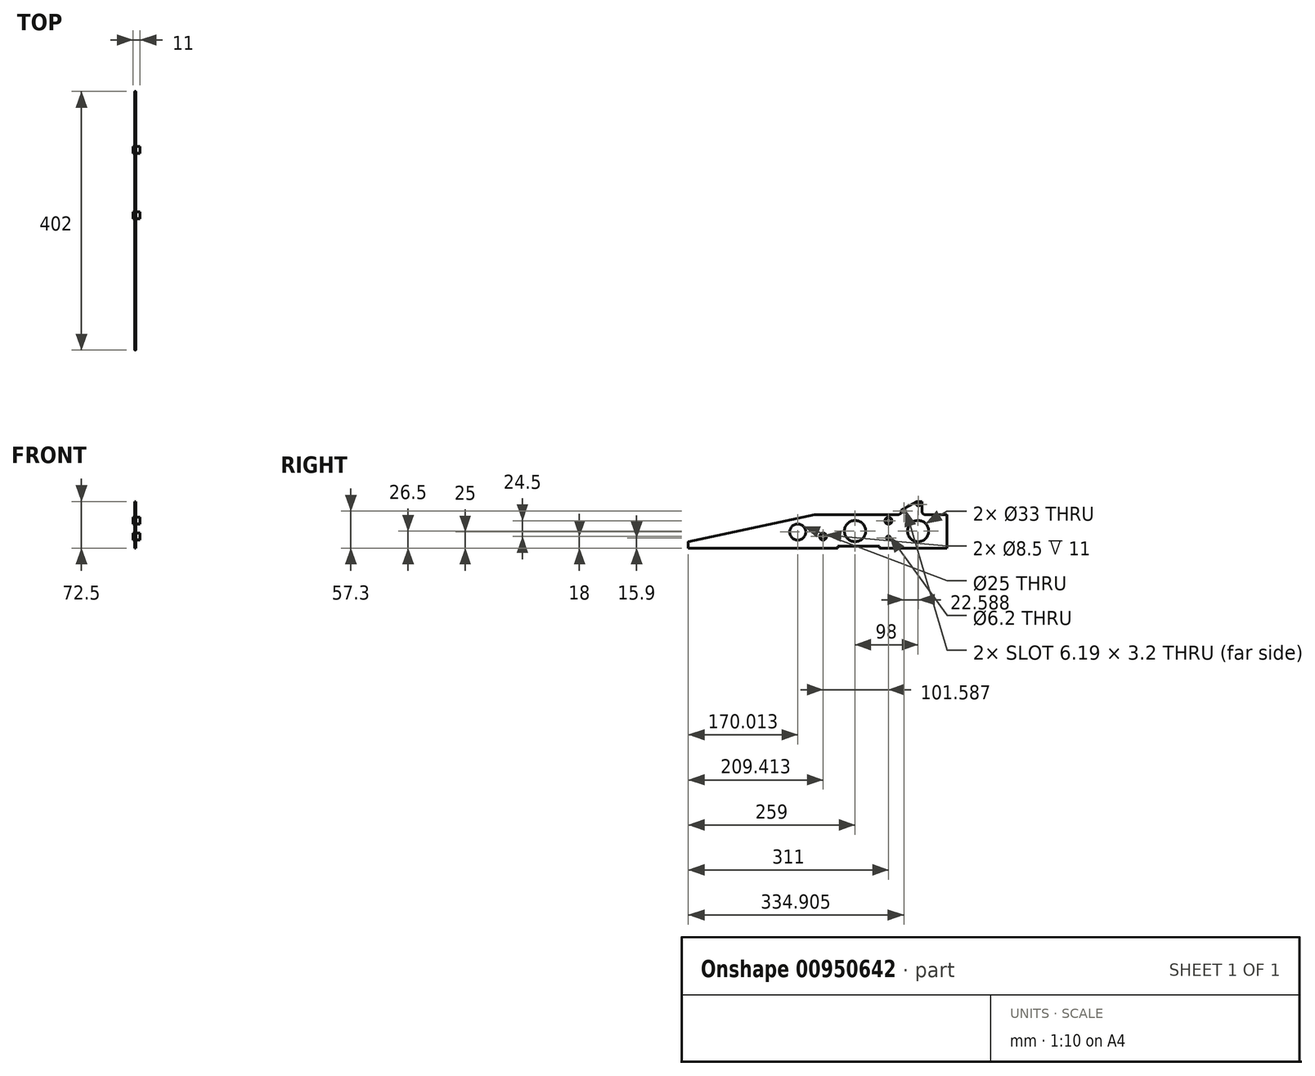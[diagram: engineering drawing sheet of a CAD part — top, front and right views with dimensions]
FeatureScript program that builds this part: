
annotation { "Feature Type Name" : "Feature", "Feature Type Description" : "" }
export const myFeature = defineFeature(function(context is Context, id is Id, definition is map)
    precondition{}
    {
        {
            var Q0;
            Q0=qCreatedBy(makeId("Right.planeOp"),FACE);
            var sketch = newSketch(context, id + "F0", { "sketchPlane" : qUnion([Q0])});
            skLineSegment(sketch, "E0.bottom", {"start": v(0, 0) * mm, "end": v(-105, 0) * mm});
            skLineSegment(sketch, "E0.top", {"start": v(-1, 52) * mm, "end": v(-34, 52) * mm});
            skLineSegment(sketch, "E0.left", {"start": v(0, 0) * mm, "end": v(0, 51) * mm});
            skLineSegment(sketch, "E0.right", {"start": v(-402, 0) * mm, "end": v(-402, 9.2) * mm});
            skLineSegment(sketch, "E1", {"start": v(-206, 125.72) * mm, "end": v(-206, -128.19) * mm, "construction": true});
            skLineSegment(sketch, "E2", {"start": v(-419.17, 10) * mm, "end": v(-375.98, 10) * mm, "construction": true});
            skLineSegment(sketch, "E3", {"start": v(-401.2, 10.17) * mm, "end": v(-206, 52) * mm});
            skCircle(sketch, "E4", {"center": v(-45, 26.5) * mm, "radius": 16.5 * mm});
            skCircle(sketch, "E5", {"center": v(-143, 26.5) * mm, "radius": 16.5 * mm});
            skCircle(sketch, "E6", {"center": v(-231.99, 25) * mm, "radius": 12.5 * mm});
            skPoint(sketch, "E7.visualSharp", {"position": v(0, 52) * mm});
            skArc(sketch, "E7.filletArc", {"start": v(0, 51) * mm, "mid": v(-0.3, 51.7) * mm, "end": v(-1, 52) * mm});
            skPoint(sketch, "E8.visualSharp", {"position": v(-402, 10) * mm});
            skArc(sketch, "E8.filletArc", {"start": v(-401.2, 10.17) * mm, "mid": v(-401.78, 9.82) * mm, "end": v(-402, 9.2) * mm});
            skLineSegment(sketch, "E9", {"start": v(-39, 72.5) * mm, "end": v(-39, 57) * mm});
            skArc(sketch, "E10", {"start": v(-39, 57) * mm, "mid": v(-37.54, 53.46) * mm, "end": v(-34, 52) * mm});
            skLineSegment(sketch, "E11", {"start": v(-71, 81.15) * mm, "end": v(-71, 57) * mm});
            skArc(sketch, "E12", {"start": v(-76, 52) * mm, "mid": v(-72.46, 53.46) * mm, "end": v(-71, 57) * mm});
            skLineSegment(sketch, "E13.trimOffspring", {"start": v(-76, 52) * mm, "end": v(-206, 52) * mm});
            skLineSegment(sketch, "E14", {"start": v(-39, 72.5) * mm, "end": v(-47, 72.5) * mm});
            skLineSegment(sketch, "E15", {"start": v(-43.01, 69.3) * mm, "end": v(-46, 69.3) * mm});
            skLineSegment(sketch, "E16", {"start": v(-43.01, 66.1) * mm, "end": v(-46, 66.1) * mm});
            skArc(sketch, "E17.trimOffspring", {"start": v(-43.01, 66.1) * mm, "mid": v(-41.41, 67.7) * mm, "end": v(-43.01, 69.3) * mm});
            skArc(sketch, "E18.trimOffspring", {"start": v(-46, 69.3) * mm, "mid": v(-47.6, 67.7) * mm, "end": v(-46, 66.1) * mm});
            skPoint(sketch, "E19.orphan", {"position": v(-47.85, 67.7) * mm});
            skLineSegment(sketch, "E20", {"start": v(-65.61, 58.9) * mm, "end": v(-68.6, 58.9) * mm});
            skLineSegment(sketch, "E21", {"start": v(-65.62, 55.7) * mm, "end": v(-68.6, 55.7) * mm});
            skArc(sketch, "E22.trimOffspring", {"start": v(-65.62, 55.7) * mm, "mid": v(-64, 57.3) * mm, "end": v(-65.61, 58.9) * mm});
            skArc(sketch, "E23.trimOffspring", {"start": v(-68.6, 58.9) * mm, "mid": v(-70.19, 57.3) * mm, "end": v(-68.6, 55.7) * mm});
            skLineSegment(sketch, "E24", {"start": v(-47, 72.5) * mm, "end": v(-71, 58.93) * mm});
            skLineSegment(sketch, "E25", {"start": v(-71, 58.93) * mm, "end": v(-71, 57) * mm});
            skCircle(sketch, "E26", {"center": v(-91, 42.5) * mm, "radius": 5.5 * mm});
            skCircle(sketch, "E27", {"center": v(-91, 42.5) * mm, "radius": 4.25 * mm});
            skLineSegment(sketch, "E28", {"start": v(-151.4, 18) * mm, "end": v(-213.42, 18) * mm, "construction": true});
            skCircle(sketch, "E29", {"center": v(-192.59, 18) * mm, "radius": 4.25 * mm});
            skCircle(sketch, "E30", {"center": v(-192.59, 18) * mm, "radius": 5.5 * mm});
            skLineSegment(sketch, "E31", {"start": v(-105, 14.17) * mm, "end": v(-105, -15.04) * mm, "construction": true});
            skLineSegment(sketch, "E32", {"start": v(-170, 8.09) * mm, "end": v(-170, -8.78) * mm, "construction": true});
            skLineSegment(sketch, "E33", {"start": v(-105, 3) * mm, "end": v(-170, 3) * mm});
            skLineSegment(sketch, "E34", {"start": v(-105, 3) * mm, "end": v(-105, 0) * mm});
            skPoint(sketch, "E34.startSnap0", {"position": v(-105, -0.44) * mm});
            skLineSegment(sketch, "E35", {"start": v(-170, 3) * mm, "end": v(-170, 0) * mm});
            skLineSegment(sketch, "E36.trimOffspring", {"start": v(-170, 0) * mm, "end": v(-402, 0) * mm});
            skCircle(sketch, "E37", {"center": v(-91, 15.9) * mm, "radius": 3.1 * mm});
            skSolve(sketch);
        }
        {
            var Q0;
            Q0=qSketchRegion(id+"F0",true);
            extrude(context, id + "F1", {"entities" : qUnion([Q0]), "depth" : 1.6 * mm, "offsetDistance" : 25 * mm});
        }
        {
            var Q0;
            Q0=makeQuery(id+"F0.imprint","IMPRINT",FACE,{"disambiguationData":[TD([[makeQuery(id+"F0.imprint","IMPRINT",EDGE,{"derivedFrom":sQuery(id+"F0.wireOp",EDGE,"E26")}),1.0]])]});
            var Q1;
            Q1=makeQuery(id+"F0.imprint","IMPRINT",FACE,{"disambiguationData":[TD([[makeQuery(id+"F0.imprint","IMPRINT",EDGE,{"derivedFrom":sQuery(id+"F0.wireOp",EDGE,"E29")}),-1.0]])]});
            extrude(context, id + "F2", {"entities" : qUnion([Q0, Q1]), "operationType" : NewBodyOperationType.ADD, "depth" : 8.5 * mm, "offsetDistance" : 25 * mm, "hasSecondDirection" : true, "secondDirectionOppositeDirection" : true, "secondDirectionDepth" : 2.5 * mm});
        }
    });
